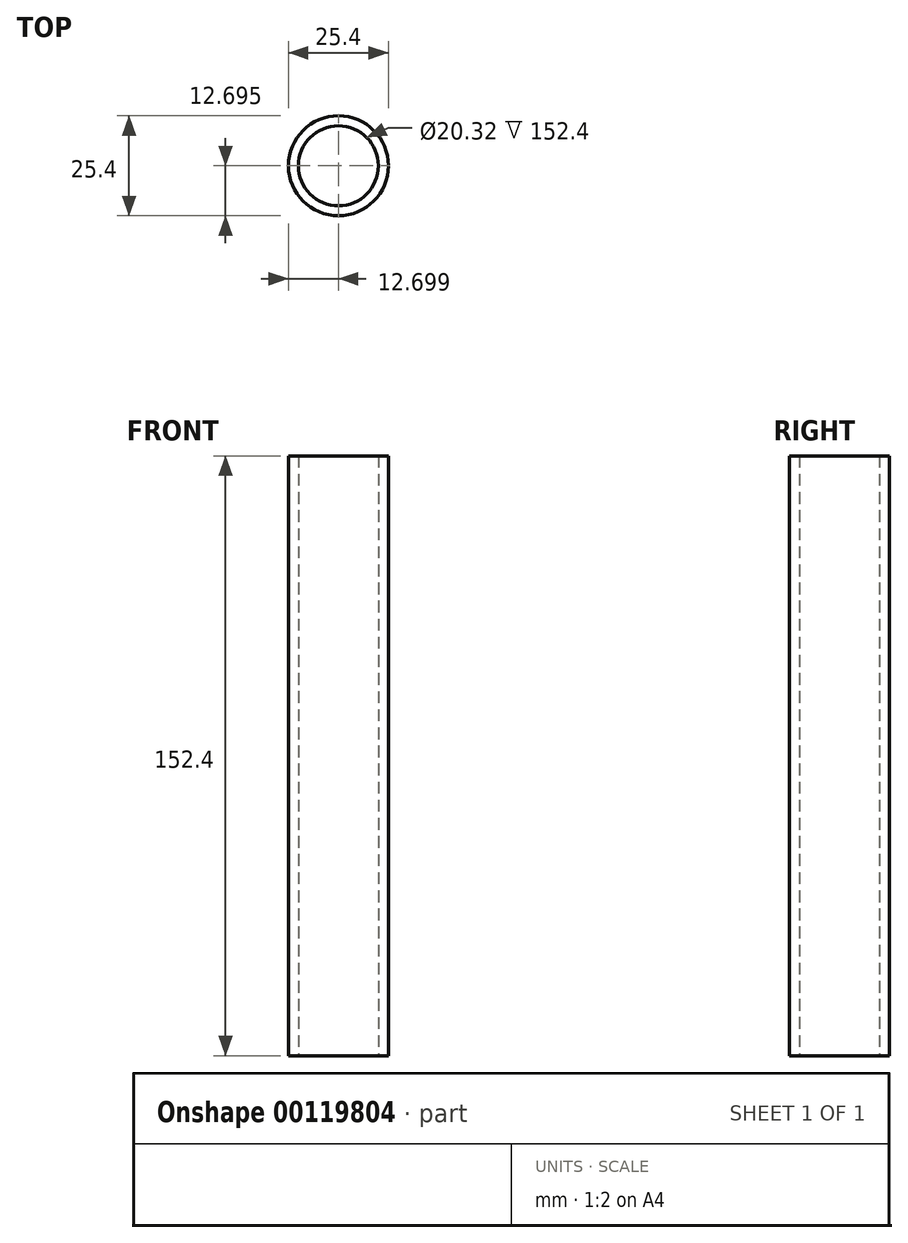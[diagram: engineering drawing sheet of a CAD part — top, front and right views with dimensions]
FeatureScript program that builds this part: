
annotation { "Feature Type Name" : "Feature", "Feature Type Description" : "" }
export const myFeature = defineFeature(function(context is Context, id is Id, definition is map)
    precondition{}
    {
        {
            var Q0;
            Q0=qCreatedBy(makeId("Top.planeOp"),FACE);
            var sketch = newSketch(context, id + "F0", { "sketchPlane" : qUnion([Q0])});
            skCircle(sketch, "E0", {"center": v(-65.22, -57.2) * mm, "radius": 12.7 * mm});
            skCircle(sketch, "E1", {"center": v(-65.22, -57.2) * mm, "radius": 10.16 * mm});
            skSolve(sketch);
        }
        {
            var Q0;
            Q0=makeQuery(id+"F0.imprint","IMPRINT",FACE,{"disambiguationData":[TD([[makeQuery(id+"F0.imprint","IMPRINT",EDGE,{"derivedFrom":sQuery(id+"F0.wireOp",EDGE,"E0")}),1.0]])]});
            extrude(context, id + "F1", {"entities" : qUnion([Q0]), "depth" : 152.4 * mm});
        }
    });
